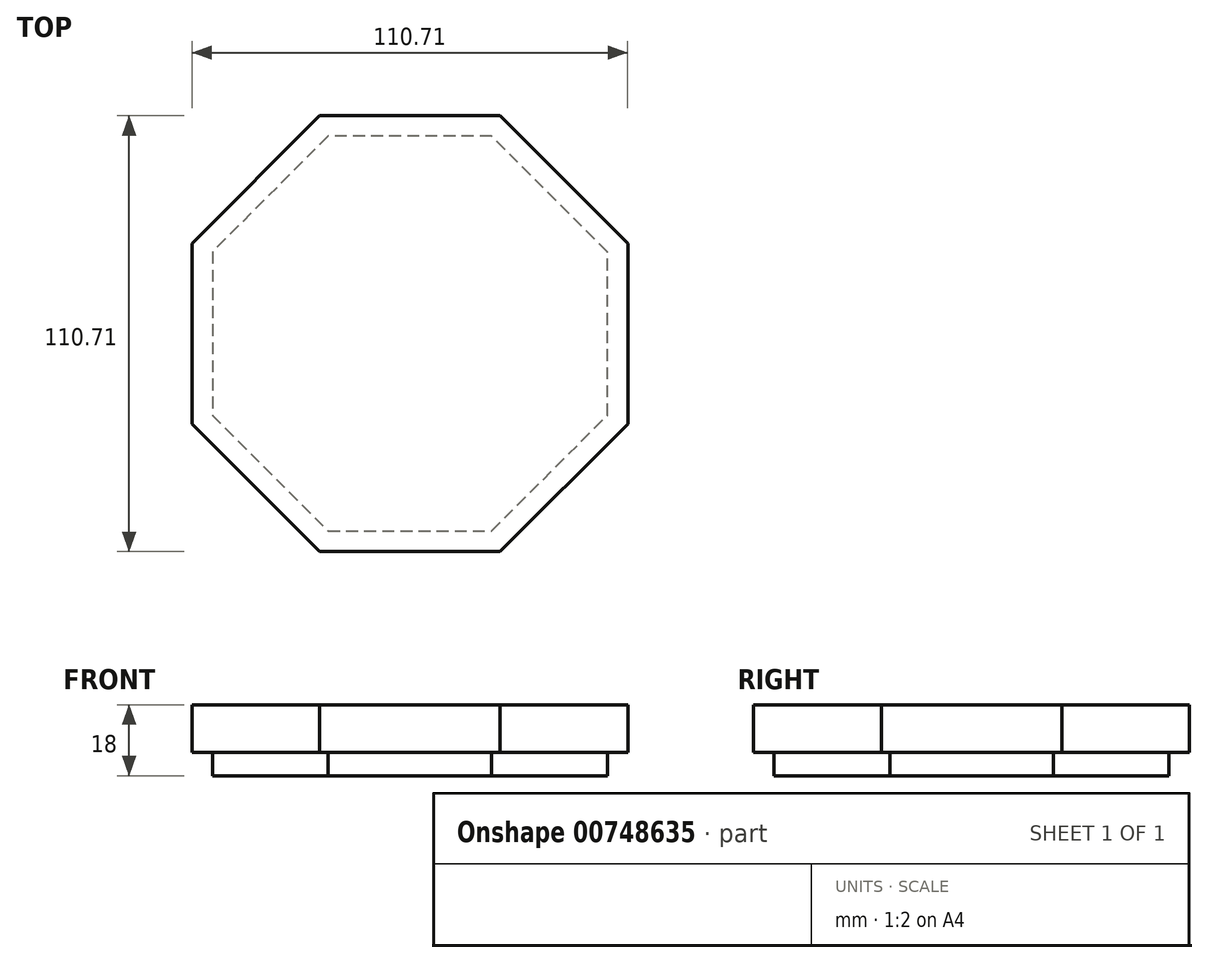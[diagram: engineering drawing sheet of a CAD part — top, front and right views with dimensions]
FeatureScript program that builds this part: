
annotation { "Feature Type Name" : "Feature", "Feature Type Description" : "" }
export const myFeature = defineFeature(function(context is Context, id is Id, definition is map)
    precondition{}
    {
        {
            var Q0;
            Q0=qCreatedBy(makeId("Top.planeOp"),FACE);
            var sketch = newSketch(context, id + "F0", { "sketchPlane" : qUnion([Q0])});
            skLineSegment(sketch, "E0.0", {"start": v(54.91, 23.37) * mm, "end": v(22.48, 55.8) * mm});
            skLineSegment(sketch, "E0.1", {"start": v(54.91, -22.48) * mm, "end": v(54.91, 23.37) * mm});
            skLineSegment(sketch, "E0.2", {"start": v(22.48, 55.8) * mm, "end": v(-23.37, 55.8) * mm});
            skLineSegment(sketch, "E0.3", {"start": v(22.48, -54.91) * mm, "end": v(54.91, -22.48) * mm});
            skLineSegment(sketch, "E0.4", {"start": v(-23.37, 55.8) * mm, "end": v(-55.8, 23.37) * mm});
            skLineSegment(sketch, "E0.5", {"start": v(-55.8, 23.37) * mm, "end": v(-55.8, -22.48) * mm});
            skLineSegment(sketch, "E0.6", {"start": v(-55.8, -22.48) * mm, "end": v(-23.37, -54.91) * mm});
            skLineSegment(sketch, "E0.7", {"start": v(-23.37, -54.91) * mm, "end": v(22.48, -54.91) * mm});
            skLineSegment(sketch, "E1.0", {"start": v(49.71, 21.22) * mm, "end": v(20.33, 50.6) * mm});
            skLineSegment(sketch, "E1.1", {"start": v(49.71, -20.33) * mm, "end": v(49.71, 21.22) * mm});
            skLineSegment(sketch, "E1.2", {"start": v(20.33, 50.6) * mm, "end": v(-21.22, 50.6) * mm});
            skLineSegment(sketch, "E1.3", {"start": v(20.33, -49.71) * mm, "end": v(49.71, -20.33) * mm});
            skLineSegment(sketch, "E1.4", {"start": v(-21.22, 50.6) * mm, "end": v(-50.6, 21.22) * mm});
            skLineSegment(sketch, "E1.5", {"start": v(-50.6, 21.22) * mm, "end": v(-50.6, -20.33) * mm});
            skLineSegment(sketch, "E1.6", {"start": v(-50.6, -20.33) * mm, "end": v(-21.22, -49.71) * mm});
            skLineSegment(sketch, "E1.7", {"start": v(-21.22, -49.71) * mm, "end": v(20.33, -49.71) * mm});
            skSolve(sketch);
        }
        {
            var Q0;
            Q0=makeQuery(id+"F0.imprint","IMPRINT",FACE,{"disambiguationData":[TD([[makeQuery(id+"F0.imprint","IMPRINT",EDGE,{"derivedFrom":sQuery(id+"F0.wireOp",EDGE,"E0.0")}),1.0]])]});
            var Q1;
            Q1=makeQuery(id+"F0.imprint","IMPRINT",FACE,{"disambiguationData":[TD([[makeQuery(id+"F0.imprint","IMPRINT",EDGE,{"derivedFrom":sQuery(id+"F0.wireOp",EDGE,"E1.0")}),1.0]])]});
            extrude(context, id + "F1", {"entities" : qUnion([Q0, Q1]), "depth" : 12 * mm, "offsetDistance" : 25 * mm});
        }
        {
            var Q0;
            Q0=makeQuery(id+"F1.opExtrude","CAP_FACE",FACE,{"disambiguationData":[OSD([sQuery(id+"F0.wireOp",EDGE,"E0.0"),sQuery(id+"F0.wireOp",EDGE,"E0.1"),sQuery(id+"F0.wireOp",EDGE,"E0.2"),sQuery(id+"F0.wireOp",EDGE,"E0.3"),sQuery(id+"F0.wireOp",EDGE,"E0.4"),sQuery(id+"F0.wireOp",EDGE,"E0.5"),sQuery(id+"F0.wireOp",EDGE,"E0.6"),sQuery(id+"F0.wireOp",EDGE,"E0.7")])],"isStart":true});
            var sketch = newSketch(context, id + "F2", { "sketchPlane" : qUnion([Q0])});
            skLineSegment(sketch, "E2.0", {"start": v(-50.6, 20.33) * mm, "end": v(-21.22, 49.71) * mm});
            skLineSegment(sketch, "E2.1", {"start": v(-50.6, -21.22) * mm, "end": v(-50.6, 20.33) * mm});
            skLineSegment(sketch, "E2.2", {"start": v(-21.22, 49.71) * mm, "end": v(20.33, 49.71) * mm});
            skLineSegment(sketch, "E2.3", {"start": v(-21.22, -50.6) * mm, "end": v(-50.6, -21.22) * mm});
            skLineSegment(sketch, "E2.4", {"start": v(20.33, 49.71) * mm, "end": v(49.71, 20.33) * mm});
            skLineSegment(sketch, "E2.5", {"start": v(49.71, 20.33) * mm, "end": v(49.71, -21.22) * mm});
            skLineSegment(sketch, "E2.6", {"start": v(49.71, -21.22) * mm, "end": v(20.33, -50.6) * mm});
            skLineSegment(sketch, "E2.7", {"start": v(20.33, -50.6) * mm, "end": v(-21.22, -50.6) * mm});
            skSolve(sketch);
        }
        {
            var Q0;
            Q0=makeQuery(id+"F2.imprint","IMPRINT",FACE,{"disambiguationData":[TD([[makeQuery(id+"F2.imprint","IMPRINT",EDGE,{"derivedFrom":sQuery(id+"F2.wireOp",EDGE,"E2.0")}),-1.0]])]});
            extrude(context, id + "F3", {"entities" : qUnion([Q0]), "operationType" : NewBodyOperationType.ADD, "depth" : 6 * mm, "offsetDistance" : 25 * mm});
        }
    });
